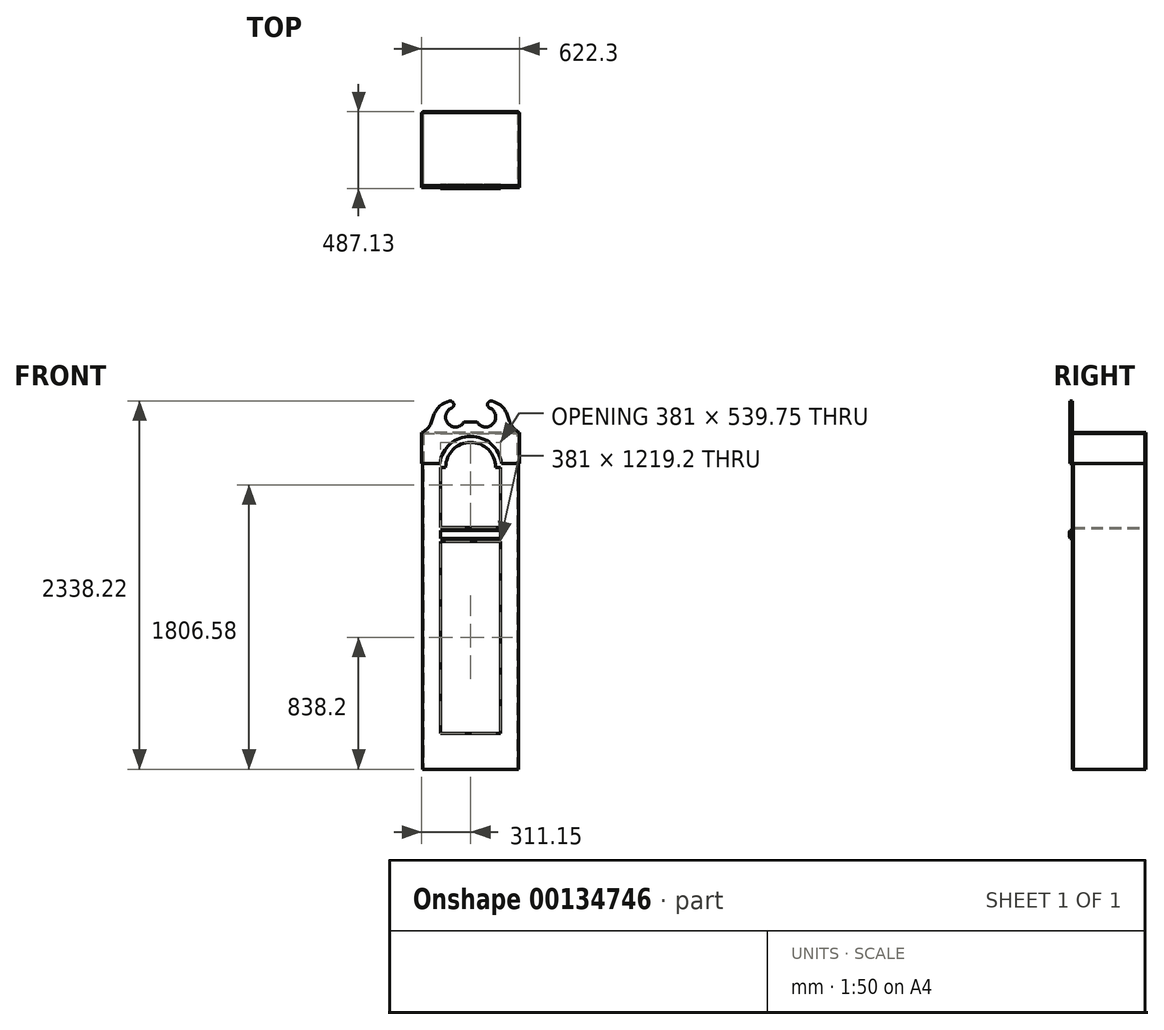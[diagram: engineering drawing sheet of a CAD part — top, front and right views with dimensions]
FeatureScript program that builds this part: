
annotation { "Feature Type Name" : "Feature", "Feature Type Description" : "" }
export const myFeature = defineFeature(function(context is Context, id is Id, definition is map)
    precondition{}
    {
        {
            var Q0;
            Q0=qCreatedBy(makeId("Front.planeOp"),FACE);
            var sketch = newSketch(context, id + "F0", { "sketchPlane" : qUnion([Q0])});
            skLineSegment(sketch, "E0.bottom", {"start": v(0, 0) * mm, "end": v(609.6, 0) * mm});
            skLineSegment(sketch, "E0.top", {"start": v(0, 2133.6) * mm, "end": v(609.6, 2133.6) * mm});
            skLineSegment(sketch, "E0.left", {"start": v(0, 0) * mm, "end": v(0, 2133.6) * mm});
            skLineSegment(sketch, "E0.right", {"start": v(609.6, 0) * mm, "end": v(609.6, 2133.6) * mm});
            skLineSegment(sketch, "E1", {"start": v(304.8, 2133.6) * mm, "end": v(304.8, 0) * mm, "construction": true});
            skLineSegment(sketch, "E2.bottom", {"start": v(495.3, 1447.8) * mm, "end": v(114.3, 1447.8) * mm});
            skLineSegment(sketch, "E2.top", {"start": v(495.3, 228.6) * mm, "end": v(114.3, 228.6) * mm});
            skLineSegment(sketch, "E2.left", {"start": v(495.3, 1447.8) * mm, "end": v(495.3, 228.6) * mm});
            skLineSegment(sketch, "E2.right", {"start": v(114.3, 1447.8) * mm, "end": v(114.3, 228.6) * mm});
            skPoint(sketch, "E2.middle", {"position": v(304.8, 838.2) * mm});
            skLineSegment(sketch, "E3.bottom", {"start": v(495.3, 1917.7) * mm, "end": v(114.3, 1917.7) * mm});
            skLineSegment(sketch, "E3.top", {"start": v(495.3, 1536.7) * mm, "end": v(114.3, 1536.7) * mm});
            skLineSegment(sketch, "E3.left", {"start": v(495.3, 1917.7) * mm, "end": v(495.3, 1536.7) * mm});
            skLineSegment(sketch, "E3.right", {"start": v(114.3, 1917.7) * mm, "end": v(114.3, 1536.7) * mm});
            skPoint(sketch, "E3.middle", {"position": v(304.8, 1727.2) * mm});
            skCircle(sketch, "E4", {"center": v(304.8, 1917.7) * mm, "radius": 158.75 * mm});
            skSolve(sketch);
        }
        {
            var Q0;
            Q0 = qSketchRegion(id + "F0", true);
            extrude(context, id + "F1", {"entities" : qUnion([Q0]), "depth" : 6.35 * mm});
        }
        {
            var Q0;
            Q0=makeQuery(id+"F1.opExtrude","SWEPT_FACE",FACE,{"disambiguationData":[OSD([sQuery(id+"F0.wireOp",EDGE,"E0.right")])]});
            var sketch = newSketch(context, id + "F2", { "sketchPlane" : qUnion([Q0])});
            skLineSegment(sketch, "E5.bottom", {"start": v(0, 0) * mm, "end": v(457.2, 0) * mm});
            skLineSegment(sketch, "E5.top", {"start": v(0, 2133.6) * mm, "end": v(457.2, 2133.6) * mm});
            skLineSegment(sketch, "E5.left", {"start": v(0, 0) * mm, "end": v(0, 2133.6) * mm});
            skLineSegment(sketch, "E5.right", {"start": v(457.2, 0) * mm, "end": v(457.2, 2133.6) * mm});
            skSolve(sketch);
        }
        {
            var Q0;
            Q0 = qSketchRegion(id + "F2", true);
            extrude(context, id + "F3", {"entities" : qUnion([Q0]), "oppositeDirection" : true, "depth" : 6.35 * mm});
        }
        {
            var Q0;
            Q0=makeQuery(id+"F1.opExtrude","SWEPT_FACE",FACE,{"disambiguationData":[OSD([sQuery(id+"F0.wireOp",EDGE,"E0.left")])]});
            var sketch = newSketch(context, id + "F4", { "sketchPlane" : qUnion([Q0])});
            skLineSegment(sketch, "E6.0.0", {"start": v(0, 0) * mm, "end": v(0, 2133.6) * mm});
            skLineSegment(sketch, "E6.0.1", {"start": v(0, 2133.6) * mm, "end": v(-457.2, 2133.6) * mm});
            skLineSegment(sketch, "E6.0.2", {"start": v(-457.2, 2133.6) * mm, "end": v(-457.2, 0) * mm});
            skLineSegment(sketch, "E6.0.3", {"start": v(-457.2, 0) * mm, "end": v(0, 0) * mm});
            skSolve(sketch);
        }
        {
            var Q0;
            Q0 = qSketchRegion(id + "F4", true);
            extrude(context, id + "F5", {"entities" : qUnion([Q0]), "oppositeDirection" : true, "depth" : 6.35 * mm});
        }
        {
            var Q0;
            Q0=makeQuery(id+"F1.opExtrude","CAP_FACE",FACE,{"disambiguationData":[OSD([sQuery(id+"F0.wireOp",EDGE,"E0.bottom"),sQuery(id+"F0.wireOp",EDGE,"E0.top"),sQuery(id+"F0.wireOp",EDGE,"E0.left"),sQuery(id+"F0.wireOp",EDGE,"E0.right"),sQuery(id+"F0.wireOp",EDGE,"E2.bottom"),sQuery(id+"F0.wireOp",EDGE,"E2.top"),sQuery(id+"F0.wireOp",EDGE,"E2.left"),sQuery(id+"F0.wireOp",EDGE,"E2.right"),sQuery(id+"F0.wireOp",EDGE,"E3.bottom"),sQuery(id+"F0.wireOp",EDGE,"E3.top"),sQuery(id+"F0.wireOp",EDGE,"E3.left"),sQuery(id+"F0.wireOp",EDGE,"E3.right"),sQuery(id+"F0.wireOp",EDGE,"E4")])],"isStart":false});
            var sketch = newSketch(context, id + "F6", { "sketchPlane" : qUnion([Q0])});
            skCircle(sketch, "E7", {"center": v(304.8, 1917.7) * mm, "radius": 196.85 * mm});
            skPoint(sketch, "E8.startSnap0", {"position": v(479.43, 1917.7) * mm});
            skPoint(sketch, "E9.endSnap0", {"position": v(130.18, 1917.7) * mm});
            skLineSegment(sketch, "E10", {"start": v(609.6, 1943.1) * mm, "end": v(609.6, 2139.95) * mm});
            skLineSegment(sketch, "E11", {"start": v(0, 1943.1) * mm, "end": v(0, 2139.95) * mm});
            skLineSegment(sketch, "E12", {"start": v(304.8, 1917.7) * mm, "end": v(304.8, 2307.6) * mm, "construction": true});
            skLineSegment(sketch, "E13", {"start": v(304.8, 2205.84) * mm, "end": v(346.58, 2205.84) * mm});
            skArc(sketch, "E14", {"start": v(346.58, 2205.84) * mm, "mid": v(448.04, 2194.36) * mm, "end": v(425.83, 2294.02) * mm});
            skArc(sketch, "E15", {"start": v(440.39, 2337.53) * mm, "mid": v(412.97, 2322.52) * mm, "end": v(425.83, 2294.02) * mm});
            skFitSpline(sketch, "E16", {"points": [v(440.39, 2337.53) * mm, v(523.54, 2279.47) * mm, v(548.8, 2220.5) * mm, v(609.6, 2139.95) * mm], "startDerivative": vector(390.02, -97.77) * mm, "endDerivative": vector(370.52, -233.27) * mm});
            skLineSegment(sketch, "E17.MirrorCS", {"start": v(304.8, 2205.84) * mm, "end": v(263.02, 2205.84) * mm});
            skArc(sketch, "E18.MirrorCS", {"start": v(263.02, 2205.84) * mm, "mid": v(161.56, 2194.36) * mm, "end": v(183.77, 2294.02) * mm});
            skArc(sketch, "E19.MirrorCS", {"start": v(169.21, 2337.53) * mm, "mid": v(196.63, 2322.52) * mm, "end": v(183.77, 2294.02) * mm});
            skFitSpline(sketch, "E20.MirrorCS", {"points": [v(169.21, 2337.53) * mm, v(86.06, 2279.47) * mm, v(60.8, 2220.5) * mm, v(0, 2139.95) * mm], "startDerivative": vector(-390.02, -97.77) * mm, "endDerivative": vector(-370.52, -233.27) * mm});
            skLineSegment(sketch, "E21", {"start": v(0, 1943.1) * mm, "end": v(609.6, 1943.1) * mm});
            skLineSegment(sketch, "E22.bottom", {"start": v(609.6, 2139.95) * mm, "end": v(615.95, 2139.95) * mm});
            skLineSegment(sketch, "E22.top", {"start": v(609.6, 1943.1) * mm, "end": v(615.95, 1943.1) * mm});
            skLineSegment(sketch, "E22.left", {"start": v(609.6, 2139.95) * mm, "end": v(609.6, 1943.1) * mm});
            skLineSegment(sketch, "E22.right", {"start": v(615.95, 2139.95) * mm, "end": v(615.95, 1943.1) * mm});
            skLineSegment(sketch, "E23.bottom", {"start": v(0, 2139.95) * mm, "end": v(-6.35, 2139.95) * mm});
            skLineSegment(sketch, "E23.top", {"start": v(0, 1943.1) * mm, "end": v(-6.35, 1943.1) * mm});
            skLineSegment(sketch, "E23.left", {"start": v(0, 2139.95) * mm, "end": v(0, 1943.1) * mm});
            skLineSegment(sketch, "E23.right", {"start": v(-6.35, 2139.95) * mm, "end": v(-6.35, 1943.1) * mm});
            skSolve(sketch);
        }
        {
            var Q0;
            Q0=makeQuery(id+"F6.imprint","IMPRINT",FACE,{"disambiguationData":[TD([[makeQuery(id+"F6.imprint","IMPRINT",EDGE,{"derivedFrom":sQuery(id+"F6.wireOp",EDGE,"E13")}),-1.0]])]});
            var Q1;
            {var subQ0=sQuery(id+"F6.wireOp",EDGE,"E22.left");Q1=makeQuery(id+"F6.imprint","IMPRINT",FACE,{"disambiguationData":[TD([[makeQuery(id+"F6.imprint","IMPRINT",EDGE,{"derivedFrom":subQ0}),1.0]])]});}
            var Q2;
            Q2=makeQuery(id+"F6.imprint","IMPRINT",FACE,{"disambiguationData":[TD([[makeQuery(id+"F6.imprint","IMPRINT",EDGE,{"derivedFrom":sQuery(id+"F6.wireOp",EDGE,"E22.bottom")}),-1.0]])]});
            var Q3;
            Q3=makeQuery(id+"F6.imprint","IMPRINT",FACE,{"disambiguationData":[TD([[makeQuery(id+"F6.imprint","IMPRINT",EDGE,{"derivedFrom":sQuery(id+"F6.wireOp",EDGE,"E23.bottom")}),1.0]])]});
            var Q4;
            {var subQ1=makeQuery(id+"F1.opExtrude","CAP_EDGE",EDGE,{"disambiguationData":[OSD([sQuery(id+"F0.wireOp",EDGE,"E0.top")])],"isStart":false});Q4=makeQuery(id+"F6.imprint","IMPRINT",FACE,{"disambiguationData":[TD([[makeQuery(id+"F6.imprint","IMPRINT",EDGE,{"derivedFrom":subQ1}),-1.0]])]});}
            extrude(context, id + "F7", {"entities" : qUnion([Q0, Q1, Q2, Q3, Q4]), "depth" : 12.7 * mm});
        }
        {
            var Q0;
            Q0=makeQuery(id+"F7.opExtrude","CAP_FACE",FACE,{"disambiguationData":[OSD([sQuery(id+"F6.wireOp",EDGE,"E7"),sQuery(id+"F6.wireOp",EDGE,"E13"),sQuery(id+"F6.wireOp",EDGE,"E14"),sQuery(id+"F6.wireOp",EDGE,"E15"),sQuery(id+"F6.wireOp",EDGE,"E16"),sQuery(id+"F6.wireOp",EDGE,"E17.MirrorCS"),sQuery(id+"F6.wireOp",EDGE,"E18.MirrorCS"),sQuery(id+"F6.wireOp",EDGE,"E19.MirrorCS"),sQuery(id+"F6.wireOp",EDGE,"E20.MirrorCS"),sQuery(id+"F6.wireOp",EDGE,"E21"),sQuery(id+"F6.wireOp",EDGE,"E22.bottom"),sQuery(id+"F6.wireOp",EDGE,"E22.top"),sQuery(id+"F6.wireOp",EDGE,"E22.right"),sQuery(id+"F6.wireOp",EDGE,"E23.bottom"),sQuery(id+"F6.wireOp",EDGE,"E23.top"),sQuery(id+"F6.wireOp",EDGE,"E23.right")])],"isStart":true});
            var sketch = newSketch(context, id + "F8", { "sketchPlane" : qUnion([Q0])});
            skLineSegment(sketch, "E24.bottom", {"start": v(-615.95, 1943.1) * mm, "end": v(-609.6, 1943.1) * mm});
            skLineSegment(sketch, "E24.top", {"start": v(-615.95, 2133.6) * mm, "end": v(-609.6, 2133.6) * mm});
            skLineSegment(sketch, "E24.left", {"start": v(-615.95, 1943.1) * mm, "end": v(-615.95, 2133.6) * mm});
            skLineSegment(sketch, "E24.right", {"start": v(-609.6, 1943.1) * mm, "end": v(-609.6, 2133.6) * mm});
            skLineSegment(sketch, "E25.top", {"start": v(6.35, 1943.1) * mm, "end": v(0, 1943.1) * mm});
            skLineSegment(sketch, "E25.left", {"start": v(6.35, 2133.6) * mm, "end": v(6.35, 1943.1) * mm});
            skLineSegment(sketch, "E25.right", {"start": v(0, 2133.6) * mm, "end": v(0, 1943.1) * mm});
            skLineSegment(sketch, "E26", {"start": v(0, 2133.6) * mm, "end": v(6.35, 2133.6) * mm});
            skSolve(sketch);
        }
        {
            var Q0;
            Q0 = qSketchRegion(id + "F8", true);
            var Q1;
            Q1=makeQuery(id+"F3.opExtrude","SWEPT_FACE",FACE,{"disambiguationData":[OSD([sQuery(id+"F2.wireOp",EDGE,"E5.right")])]});
            extrude(context, id + "F9", {"entities" : qUnion([Q0]), "endBound" : BoundingType.UP_TO_SURFACE, "endBoundEntityFace" : qUnion([Q1]), "depth" : 25.4 * mm});
        }
        {
            var Q0;
            Q0=makeQuery(id+"F1.opExtrude","SWEPT_FACE",FACE,{"disambiguationData":[OSD([sQuery(id+"F0.wireOp",EDGE,"E0.top")])]});
            var sketch = newSketch(context, id + "F10", { "sketchPlane" : qUnion([Q0])});
            skLineSegment(sketch, "E27.bottom", {"start": v(615.95, -6.35) * mm, "end": v(-6.35, -6.35) * mm});
            skLineSegment(sketch, "E27.top", {"start": v(615.95, 457.2) * mm, "end": v(-6.35, 457.2) * mm});
            skLineSegment(sketch, "E27.left", {"start": v(615.95, -6.35) * mm, "end": v(615.95, 457.2) * mm});
            skLineSegment(sketch, "E27.right", {"start": v(-6.35, -6.35) * mm, "end": v(-6.35, 457.2) * mm});
            skSolve(sketch);
        }
        {
            var Q0;
            Q0 = qSketchRegion(id + "F10", true);
            extrude(context, id + "F11", {"entities" : qUnion([Q0]), "depth" : 6.35 * mm});
        }
        {
            var Q0;
            Q0=makeQuery(id+"F1.opExtrude","SWEPT_FACE",FACE,{"disambiguationData":[OSD([sQuery(id+"F0.wireOp",EDGE,"E0.bottom")])]});
            var sketch = newSketch(context, id + "F12", { "sketchPlane" : qUnion([Q0])});
            skLineSegment(sketch, "E28.top", {"start": v(6.35, -457.2) * mm, "end": v(603.25, -457.2) * mm});
            skLineSegment(sketch, "E28.left", {"start": v(6.35, 0) * mm, "end": v(6.35, -457.2) * mm});
            skLineSegment(sketch, "E28.right", {"start": v(603.25, 0) * mm, "end": v(603.25, -457.2) * mm});
            skLineSegment(sketch, "E29", {"start": v(603.25, 0) * mm, "end": v(6.35, 0) * mm});
            skSolve(sketch);
        }
        {
            var Q0;
            Q0 = qSketchRegion(id + "F12", true);
            extrude(context, id + "F13", {"entities" : qUnion([Q0]), "oppositeDirection" : true, "depth" : 6.35 * mm});
        }
        {
            var Q0;
            Q0=makeQuery(id+"F1.opExtrude","CAP_FACE",FACE,{"disambiguationData":[OSD([sQuery(id+"F0.wireOp",EDGE,"E0.bottom"),sQuery(id+"F0.wireOp",EDGE,"E0.top"),sQuery(id+"F0.wireOp",EDGE,"E0.left"),sQuery(id+"F0.wireOp",EDGE,"E0.right"),sQuery(id+"F0.wireOp",EDGE,"E2.bottom"),sQuery(id+"F0.wireOp",EDGE,"E2.top"),sQuery(id+"F0.wireOp",EDGE,"E2.left"),sQuery(id+"F0.wireOp",EDGE,"E2.right"),sQuery(id+"F0.wireOp",EDGE,"E3.bottom"),sQuery(id+"F0.wireOp",EDGE,"E3.top"),sQuery(id+"F0.wireOp",EDGE,"E3.left"),sQuery(id+"F0.wireOp",EDGE,"E3.right"),sQuery(id+"F0.wireOp",EDGE,"E4")])],"isStart":true});
            var sketch = newSketch(context, id + "F14", { "sketchPlane" : qUnion([Q0])});
            skLineSegment(sketch, "E30", {"start": v(-609.6, 0) * mm, "end": v(-603.25, 0) * mm, "construction": true});
            skLineSegment(sketch, "E31", {"start": v(-606.43, 0) * mm, "end": v(-606.43, 2133.6) * mm, "construction": true});
            skPoint(sketch, "E31.endSnap0", {"position": v(-304.8, 2133.6) * mm});
            skLineSegment(sketch, "E32", {"start": v(0, 0) * mm, "end": v(-6.35, 0) * mm, "construction": true});
            skLineSegment(sketch, "E33", {"start": v(-3.18, 0) * mm, "end": v(-3.18, 2133.6) * mm, "construction": true});
            skLineSegment(sketch, "E34.bottom", {"start": v(-606.43, 1536.7) * mm, "end": v(-3.17, 1536.7) * mm});
            skLineSegment(sketch, "E34.top", {"start": v(-606.43, 1530.35) * mm, "end": v(-3.17, 1530.35) * mm});
            skLineSegment(sketch, "E34.left", {"start": v(-606.43, 1536.7) * mm, "end": v(-606.43, 1530.35) * mm});
            skLineSegment(sketch, "E34.right", {"start": v(-3.18, 1536.7) * mm, "end": v(-3.18, 1530.35) * mm});
            skSolve(sketch);
        }
        {
            var Q0;
            Q0 = qSketchRegion(id + "F14", true);
            var Q1;
            Q1=makeQuery(id+"F3.opExtrude","SWEPT_FACE",FACE,{"disambiguationData":[OSD([sQuery(id+"F2.wireOp",EDGE,"E5.right")])]});
            extrude(context, id + "F15", {"entities" : qUnion([Q0]), "operationType" : NewBodyOperationType.REMOVE, "endBound" : BoundingType.UP_TO_SURFACE, "endBoundEntityFace" : qUnion([Q1]), "depth" : 25.4 * mm});
        }
        {
            var Q0;
            Q0=makeQuery(id+"F1.opExtrude","SWEPT_FACE",FACE,{"disambiguationData":[OSD([sQuery(id+"F0.wireOp",EDGE,"E3.left")])]});
            var sketch = newSketch(context, id + "F16", { "sketchPlane" : qUnion([Q0])});
            skLineSegment(sketch, "E35", {"start": v(6.35, 1536.7) * mm, "end": v(6.35, 1447.8) * mm, "construction": true});
            skLineSegment(sketch, "E36", {"start": v(6.35, 1492.25) * mm, "end": v(49.07, 1492.25) * mm, "construction": true});
            skLineSegment(sketch, "E37", {"start": v(6.35, 1517.65) * mm, "end": v(6.35, 1466.85) * mm});
            skLineSegment(sketch, "E38", {"start": v(6.35, 1517.65) * mm, "end": v(20.64, 1517.65) * mm});
            skLineSegment(sketch, "E39", {"start": v(20.64, 1517.65) * mm, "end": v(20.64, 1466.85) * mm});
            skLineSegment(sketch, "E40", {"start": v(20.64, 1466.85) * mm, "end": v(6.35, 1466.85) * mm});
            skArc(sketch, "E41", {"start": v(20.64, 1466.85) * mm, "mid": v(23.58, 1492.25) * mm, "end": v(20.64, 1517.65) * mm});
            skSolve(sketch);
        }
        {
            var Q0;
            Q0 = qSketchRegion(id + "F16", true);
            var Q1;
            Q1=makeQuery(id+"F1.opExtrude","SWEPT_FACE",FACE,{"disambiguationData":[OSD([sQuery(id+"F0.wireOp",EDGE,"E3.right")])]});
            extrude(context, id + "F17", {"entities" : qUnion([Q0]), "endBound" : BoundingType.UP_TO_SURFACE, "endBoundEntityFace" : qUnion([Q1]), "depth" : 25.4 * mm});
        }
        {
            var Q0;
            Q0=makeQuery(id+"F11.opExtrude","SWEPT_FACE",FACE,{"disambiguationData":[OSD([sQuery(id+"F10.wireOp",EDGE,"E27.top")])]});
            var sketch = newSketch(context, id + "F18", { "sketchPlane" : qUnion([Q0])});
            skLineSegment(sketch, "E42.bottom", {"start": v(-609.6, 2139.95) * mm, "end": v(0, 2139.95) * mm});
            skLineSegment(sketch, "E42.top", {"start": v(-609.6, 0) * mm, "end": v(0, 0) * mm});
            skLineSegment(sketch, "E42.left", {"start": v(-609.6, 2139.95) * mm, "end": v(-609.6, 0) * mm});
            skLineSegment(sketch, "E42.right", {"start": v(0, 2139.95) * mm, "end": v(0, 0) * mm});
            skSolve(sketch);
        }
        {
            var Q0;
            Q0 = qSketchRegion(id + "F18", true);
            extrude(context, id + "F19", {"entities" : qUnion([Q0]), "depth" : 6.35 * mm});
        }
    });
